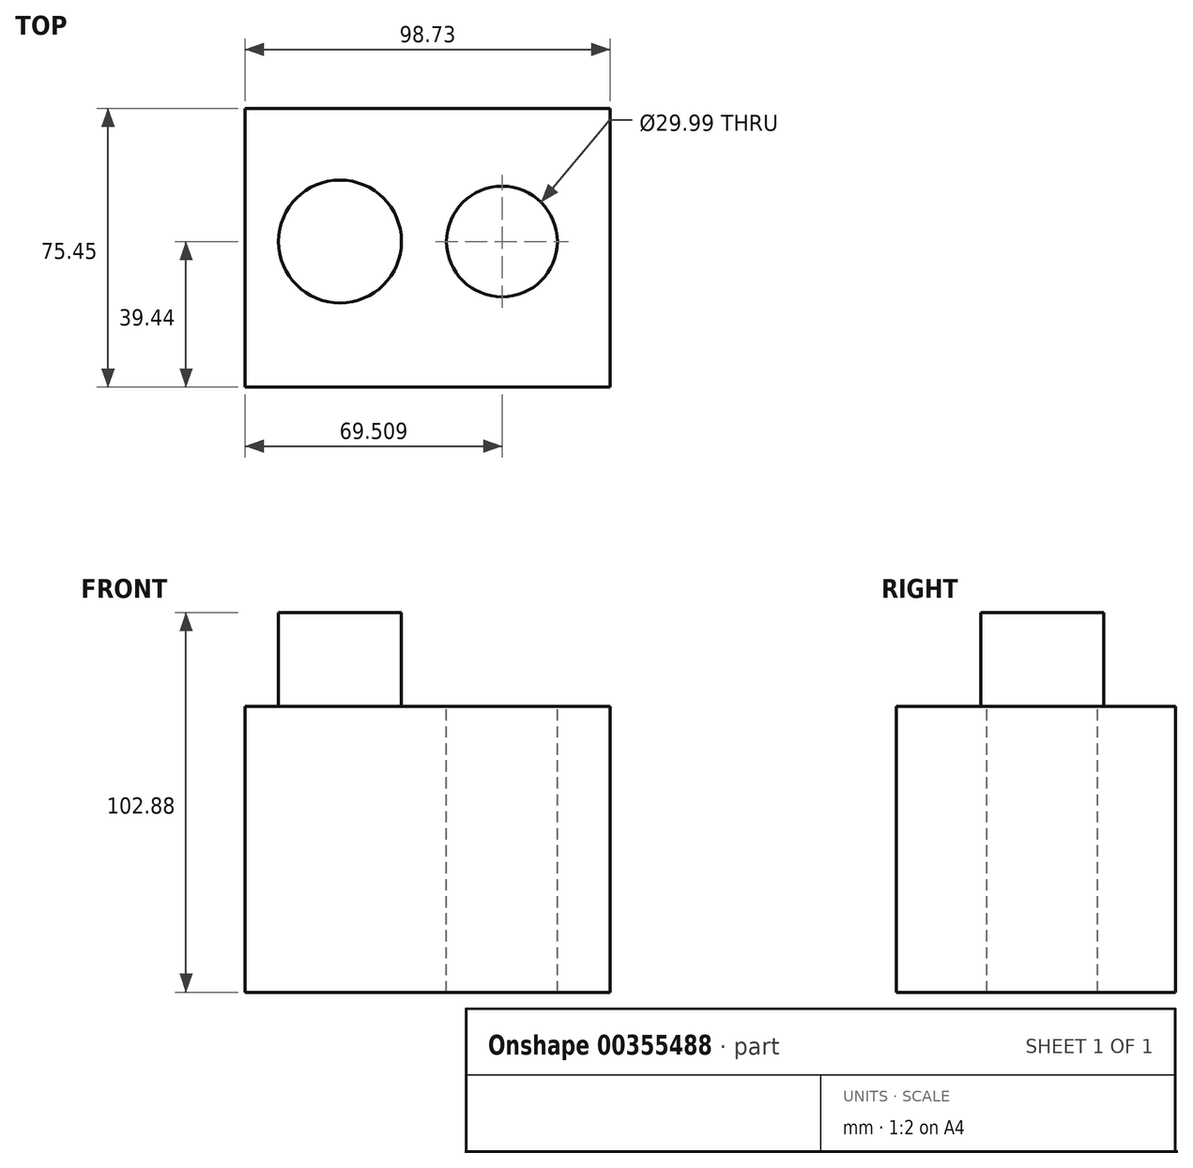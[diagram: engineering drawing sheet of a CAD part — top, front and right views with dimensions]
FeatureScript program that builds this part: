
annotation { "Feature Type Name" : "Feature", "Feature Type Description" : "" }
export const myFeature = defineFeature(function(context is Context, id is Id, definition is map)
    precondition{}
    {
        {
            var Q0;
            Q0=qCreatedBy(makeId("Top.planeOp"),FACE);
            var sketch = newSketch(context, id + "F0", { "sketchPlane" : qUnion([Q0])});
            skLineSegment(sketch, "E0.bottom", {"start": v(-43.32, 36.01) * mm, "end": v(55.41, 36.01) * mm});
            skLineSegment(sketch, "E0.top", {"start": v(-43.32, -39.44) * mm, "end": v(55.41, -39.44) * mm});
            skLineSegment(sketch, "E0.left", {"start": v(-43.32, 36.01) * mm, "end": v(-43.32, -39.44) * mm});
            skLineSegment(sketch, "E0.right", {"start": v(55.41, 36.01) * mm, "end": v(55.41, -39.44) * mm});
            skSolve(sketch);
        }
        {
            var Q0;
            Q0=makeQuery(id+"F0.imprint","IMPRINT",FACE,{"disambiguationData":[TD([[makeQuery(id+"F0.imprint","IMPRINT",EDGE,{"derivedFrom":sQuery(id+"F0.wireOp",EDGE,"E0.bottom")}),-1.0]])]});
            extrude(context, id + "F1", {"entities" : qUnion([Q0]), "depth" : 77.48 * mm});
        }
        {
            var Q0;
            Q0=makeQuery(id+"F1.opExtrude","CAP_FACE",FACE,{"disambiguationData":[OSD([sQuery(id+"F0.wireOp",EDGE,"E0.bottom"),sQuery(id+"F0.wireOp",EDGE,"E0.top"),sQuery(id+"F0.wireOp",EDGE,"E0.left"),sQuery(id+"F0.wireOp",EDGE,"E0.right")])],"isStart":false});
            var sketch = newSketch(context, id + "F2", { "sketchPlane" : qUnion([Q0])});
            skCircle(sketch, "E1", {"center": v(26.19, 0) * mm, "radius": 15 * mm});
            skSolve(sketch);
        }
        {
            var Q0;
            Q0 = qSketchRegion(id + "F2", true);
            extrude(context, id + "F3", {"entities" : qUnion([Q0]), "operationType" : NewBodyOperationType.REMOVE, "oppositeDirection" : true, "depth" : 122.46 * mm});
        }
        {
            var Q0;
            Q0=makeQuery(id+"F1.opExtrude","CAP_FACE",FACE,{"disambiguationData":[OSD([sQuery(id+"F0.wireOp",EDGE,"E0.bottom"),sQuery(id+"F0.wireOp",EDGE,"E0.top"),sQuery(id+"F0.wireOp",EDGE,"E0.left"),sQuery(id+"F0.wireOp",EDGE,"E0.right")])],"isStart":false});
            var sketch = newSketch(context, id + "F4", { "sketchPlane" : qUnion([Q0])});
            skCircle(sketch, "E2", {"center": v(-17.65, 0) * mm, "radius": 16.64 * mm});
            skSolve(sketch);
        }
        {
            var Q0;
            Q0=makeQuery(id+"F4.imprint","IMPRINT",FACE,{"disambiguationData":[TD([[makeQuery(id+"F4.imprint","IMPRINT",EDGE,{"derivedFrom":sQuery(id+"F4.wireOp",EDGE,"E2")}),1.0]])]});
            extrude(context, id + "F5", {"entities" : qUnion([Q0]), "operationType" : NewBodyOperationType.ADD, "depth" : 25.4 * mm});
        }
    });
